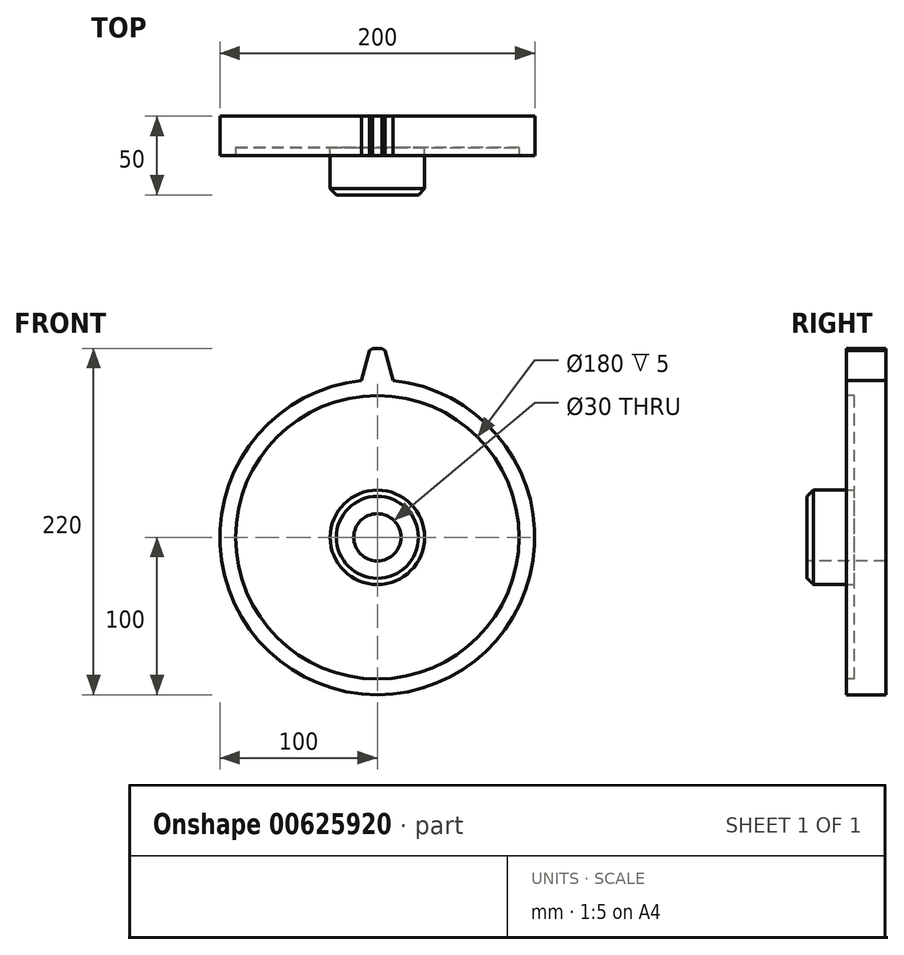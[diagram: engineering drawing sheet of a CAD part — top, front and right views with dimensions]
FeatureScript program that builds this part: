
annotation { "Feature Type Name" : "Feature", "Feature Type Description" : "" }
export const myFeature = defineFeature(function(context is Context, id is Id, definition is map)
    precondition{}
    {
        {
            var Q0;
            Q0=qCreatedBy(makeId("Front.planeOp"),FACE);
            var sketch = newSketch(context, id + "F0", { "sketchPlane" : qUnion([Q0])});
            skCircle(sketch, "E0", {"center": v(0, 0) * mm, "radius": 100 * mm});
            skSolve(sketch);
        }
        {
            var Q0;
            Q0 = qSketchRegion(id + "F0", true);
            extrude(context, id + "F1", {"entities" : qUnion([Q0]), "depth" : 25 * mm, "offsetDistance" : 25 * mm});
        }
        {
            var Q0;
            Q0=makeQuery(id+"F1.opExtrude","CAP_FACE",FACE,{"disambiguationData":[OSD([sQuery(id+"F0.wireOp",EDGE,"E0")])],"isStart":false});
            var sketch = newSketch(context, id + "F2", { "sketchPlane" : qUnion([Q0])});
            skCircle(sketch, "E1", {"center": v(0, 0) * mm, "radius": 120 * mm, "construction": true});
            skLineSegment(sketch, "E2", {"start": v(4.5, 120) * mm, "end": v(-4.5, 120) * mm});
            skPoint(sketch, "E3", {"position": v(0, 120) * mm});
            skLineSegment(sketch, "E4", {"start": v(-4.5, 120) * mm, "end": v(-10, 99.5) * mm});
            skLineSegment(sketch, "E5", {"start": v(4.5, 120) * mm, "end": v(10, 99.5) * mm});
            skLineSegment(sketch, "E6", {"start": v(-10, 99.5) * mm, "end": v(10, 99.5) * mm});
            skSolve(sketch);
        }
        {
            var Q0;
            Q0=makeQuery(id+"F2.imprint","IMPRINT",FACE,{"disambiguationData":[TD([[makeQuery(id+"F2.imprint","IMPRINT",EDGE,{"derivedFrom":sQuery(id+"F2.wireOp",EDGE,"E2")}),1.0]])]});
            extrude(context, id + "F3", {"entities" : qUnion([Q0]), "operationType" : NewBodyOperationType.ADD, "oppositeDirection" : true, "depth" : 25 * mm, "offsetDistance" : 25 * mm});
        }
        {
            var Q0;
            Q0=makeQuery(id+"F3.opExtrude","SWEPT_EDGE",EDGE,{"disambiguationData":[OSD([sQuery(id+"F2.wireOp",EDGE,"E2"),sQuery(id+"F2.wireOp",EDGE,"E5")])]});
            var Q1;
            Q1=makeQuery(id+"F3.opExtrude","SWEPT_EDGE",EDGE,{"disambiguationData":[OSD([sQuery(id+"F2.wireOp",EDGE,"E2"),sQuery(id+"F2.wireOp",EDGE,"E4")])]});
            chamfer(context, id + "F4", {"entities" : qUnion([Q0, Q1]), "width" : 2 * mm, "tangentPropagation" : true});
        }
        {
            var Q0;
            Q0=makeQuery(id+"F3.opExtrude","SWEPT_EDGE",EDGE,{"disambiguationData":[OSD([sQuery(id+"F0.wireOp",EDGE,"E0"),sQuery(id+"F2.wireOp",EDGE,"E4"),sQuery(id+"F2.wireOp",EDGE,"E6")])]});
            var Q1;
            Q1=makeQuery(id+"F3.opExtrude","SWEPT_EDGE",EDGE,{"disambiguationData":[OSD([sQuery(id+"F0.wireOp",EDGE,"E0"),sQuery(id+"F2.wireOp",EDGE,"E5"),sQuery(id+"F2.wireOp",EDGE,"E6")])]});
            fillet(context, id + "F5", {"entities" : qUnion([Q0, Q1]), "radius" : 5 * mm, "tangentPropagation" : true, "allowEdgeOverflow" : false});
        }
        {
            var Q0;
            {var subQ0=sQuery(id+"F2.wireOp",EDGE,"E5");var subQ1=sQuery(id+"F2.wireOp",EDGE,"E4");var subQ2=sQuery(id+"F2.wireOp",EDGE,"E2");var subQ3=sQuery(id+"F0.wireOp",EDGE,"E0");Q0=makeQuery(id+"F1aVIN3etHBw0Ek_1.19.F3.boolean.opBoolean","MERGE",FACE,{"derivedFrom":[makeQuery(id+"F1aVIN3etHBw0Ek_1.18.F3.boolean.opBoolean","MERGE",FACE,{"derivedFrom":[makeQuery(id+"F1aVIN3etHBw0Ek_1.17.F3.boolean.opBoolean","MERGE",FACE,{"derivedFrom":[makeQuery(id+"F1aVIN3etHBw0Ek_1.16.F3.boolean.opBoolean","MERGE",FACE,{"derivedFrom":[makeQuery(id+"F1aVIN3etHBw0Ek_1.15.F3.boolean.opBoolean","MERGE",FACE,{"derivedFrom":[makeQuery(id+"F1aVIN3etHBw0Ek_1.14.F3.boolean.opBoolean","MERGE",FACE,{"derivedFrom":[makeQuery(id+"F1aVIN3etHBw0Ek_1.13.F3.boolean.opBoolean","MERGE",FACE,{"derivedFrom":[makeQuery(id+"F1aVIN3etHBw0Ek_1.12.F3.boolean.opBoolean","MERGE",FACE,{"derivedFrom":[makeQuery(id+"F1aVIN3etHBw0Ek_1.11.F3.boolean.opBoolean","MERGE",FACE,{"derivedFrom":[makeQuery(id+"F1aVIN3etHBw0Ek_1.10.F3.boolean.opBoolean","MERGE",FACE,{"derivedFrom":[makeQuery(id+"F1aVIN3etHBw0Ek_1.9.F3.boolean.opBoolean","MERGE",FACE,{"derivedFrom":[makeQuery(id+"F1aVIN3etHBw0Ek_1.8.F3.boolean.opBoolean","MERGE",FACE,{"derivedFrom":[makeQuery(id+"F1aVIN3etHBw0Ek_1.7.F3.boolean.opBoolean","MERGE",FACE,{"derivedFrom":[makeQuery(id+"F1aVIN3etHBw0Ek_1.6.F3.boolean.opBoolean","MERGE",FACE,{"derivedFrom":[makeQuery(id+"F1aVIN3etHBw0Ek_1.5.F3.boolean.opBoolean","MERGE",FACE,{"derivedFrom":[makeQuery(id+"F1aVIN3etHBw0Ek_1.4.F3.boolean.opBoolean","MERGE",FACE,{"derivedFrom":[makeQuery(id+"F1aVIN3etHBw0Ek_1.3.F3.boolean.opBoolean","MERGE",FACE,{"derivedFrom":[makeQuery(id+"F1aVIN3etHBw0Ek_1.2.F3.boolean.opBoolean","MERGE",FACE,{"derivedFrom":[makeQuery(id+"F1aVIN3etHBw0Ek_1.1.F3.boolean.opBoolean","MERGE",FACE,{"derivedFrom":[makeQuery(id+"F3.boolean.opBoolean","MERGE",FACE,{"derivedFrom":[makeQuery(id+"F1.opExtrude","CAP_FACE",FACE,{"disambiguationData":[OSD([subQ3])],"isStart":false}),makeQuery(id+"F3.opExtrude","CAP_FACE",FACE,{"disambiguationData":[OSD([subQ3,subQ2,subQ1,subQ0])],"isStart":true})]}),makeQuery(id+"F1aVIN3etHBw0Ek_1.1.F3.opExtrude","CAP_FACE",FACE,{"disambiguationData":[OSD([subQ3,subQ2,subQ1,subQ0])],"isStart":true})]}),makeQuery(id+"F1aVIN3etHBw0Ek_1.2.F3.opExtrude","CAP_FACE",FACE,{"disambiguationData":[OSD([subQ3,subQ2,subQ1,subQ0])],"isStart":true})]}),makeQuery(id+"F1aVIN3etHBw0Ek_1.3.F3.opExtrude","CAP_FACE",FACE,{"disambiguationData":[OSD([subQ3,subQ2,subQ1,subQ0])],"isStart":true})]}),makeQuery(id+"F1aVIN3etHBw0Ek_1.4.F3.opExtrude","CAP_FACE",FACE,{"disambiguationData":[OSD([subQ3,subQ2,subQ1,subQ0])],"isStart":true})]}),makeQuery(id+"F1aVIN3etHBw0Ek_1.5.F3.opExtrude","CAP_FACE",FACE,{"disambiguationData":[OSD([subQ3,subQ2,subQ1,subQ0])],"isStart":true})]}),makeQuery(id+"F1aVIN3etHBw0Ek_1.6.F3.opExtrude","CAP_FACE",FACE,{"disambiguationData":[OSD([subQ3,subQ2,subQ1,subQ0])],"isStart":true})]}),makeQuery(id+"F1aVIN3etHBw0Ek_1.7.F3.opExtrude","CAP_FACE",FACE,{"disambiguationData":[OSD([subQ3,subQ2,subQ1,subQ0])],"isStart":true})]}),makeQuery(id+"F1aVIN3etHBw0Ek_1.8.F3.opExtrude","CAP_FACE",FACE,{"disambiguationData":[OSD([subQ3,subQ2,subQ1,subQ0])],"isStart":true})]}),makeQuery(id+"F1aVIN3etHBw0Ek_1.9.F3.opExtrude","CAP_FACE",FACE,{"disambiguationData":[OSD([subQ3,subQ2,subQ1,subQ0])],"isStart":true})]}),makeQuery(id+"F1aVIN3etHBw0Ek_1.10.F3.opExtrude","CAP_FACE",FACE,{"disambiguationData":[OSD([subQ3,subQ2,subQ1,subQ0])],"isStart":true})]}),makeQuery(id+"F1aVIN3etHBw0Ek_1.11.F3.opExtrude","CAP_FACE",FACE,{"disambiguationData":[OSD([subQ3,subQ2,subQ1,subQ0])],"isStart":true})]}),makeQuery(id+"F1aVIN3etHBw0Ek_1.12.F3.opExtrude","CAP_FACE",FACE,{"disambiguationData":[OSD([subQ3,subQ2,subQ1,subQ0])],"isStart":true})]}),makeQuery(id+"F1aVIN3etHBw0Ek_1.13.F3.opExtrude","CAP_FACE",FACE,{"disambiguationData":[OSD([subQ3,subQ2,subQ1,subQ0])],"isStart":true})]}),makeQuery(id+"F1aVIN3etHBw0Ek_1.14.F3.opExtrude","CAP_FACE",FACE,{"disambiguationData":[OSD([subQ3,subQ2,subQ1,subQ0])],"isStart":true})]}),makeQuery(id+"F1aVIN3etHBw0Ek_1.15.F3.opExtrude","CAP_FACE",FACE,{"disambiguationData":[OSD([subQ3,subQ2,subQ1,subQ0])],"isStart":true})]}),makeQuery(id+"F1aVIN3etHBw0Ek_1.16.F3.opExtrude","CAP_FACE",FACE,{"disambiguationData":[OSD([subQ3,subQ2,subQ1,subQ0])],"isStart":true})]}),makeQuery(id+"F1aVIN3etHBw0Ek_1.17.F3.opExtrude","CAP_FACE",FACE,{"disambiguationData":[OSD([subQ3,subQ2,subQ1,subQ0])],"isStart":true})]}),makeQuery(id+"F1aVIN3etHBw0Ek_1.18.F3.opExtrude","CAP_FACE",FACE,{"disambiguationData":[OSD([subQ3,subQ2,subQ1,subQ0])],"isStart":true})]}),makeQuery(id+"F1aVIN3etHBw0Ek_1.19.F3.opExtrude","CAP_FACE",FACE,{"disambiguationData":[OSD([subQ3,subQ2,subQ1,subQ0])],"isStart":true})]});}
            var sketch = newSketch(context, id + "F6", { "sketchPlane" : qUnion([Q0])});
            skCircle(sketch, "E7", {"center": v(0, 0) * mm, "radius": 90 * mm});
            skSolve(sketch);
        }
        {
            var Q0;
            Q0 = qSketchRegion(id + "F6", true);
            extrude(context, id + "F7", {"entities" : qUnion([Q0]), "operationType" : NewBodyOperationType.REMOVE, "oppositeDirection" : true, "depth" : 5 * mm, "offsetDistance" : 25 * mm});
        }
        {
            var Q0;
            Q0=makeQuery(id+"F7.boolean.opBoolean","COPY",FACE,{"derivedFrom":makeQuery(id+"F7.opExtrude","CAP_FACE",FACE,{"disambiguationData":[OSD([sQuery(id+"F6.wireOp",EDGE,"E7")])],"isStart":false})});
            var sketch = newSketch(context, id + "F8", { "sketchPlane" : qUnion([Q0])});
            skCircle(sketch, "E8", {"center": v(0, 0) * mm, "radius": 30 * mm});
            skSolve(sketch);
        }
        {
            var Q0;
            Q0 = qSketchRegion(id + "F8", true);
            extrude(context, id + "F9", {"entities" : qUnion([Q0]), "operationType" : NewBodyOperationType.ADD, "depth" : 30 * mm, "offsetDistance" : 25 * mm});
        }
        {
            var Q0;
            Q0=makeQuery(id+"F9.opExtrude","CAP_FACE",FACE,{"disambiguationData":[OSD([sQuery(id+"F8.wireOp",EDGE,"E8")])],"isStart":false});
            var sketch = newSketch(context, id + "F10", { "sketchPlane" : qUnion([Q0])});
            skCircle(sketch, "E9", {"center": v(0, 0) * mm, "radius": 15 * mm});
            skSolve(sketch);
        }
        {
            var Q0;
            Q0 = qSketchRegion(id + "F10", true);
            extrude(context, id + "F11", {"entities" : qUnion([Q0]), "operationType" : NewBodyOperationType.REMOVE, "endBound" : BoundingType.THROUGH_ALL, "oppositeDirection" : true, "depth" : 25 * mm, "offsetDistance" : 25 * mm});
        }
        {
            var Q0;
            Q0=makeQuery(id+"F9.opExtrude","CAP_EDGE",EDGE,{"disambiguationData":[OSD([sQuery(id+"F8.wireOp",EDGE,"E8")])],"isStart":false});
            var Q1;
            Q1=makeQuery(id+"F11.boolean.opBoolean","COPY",EDGE,{"derivedFrom":makeQuery(id+"F11.opExtrude","CAP_EDGE",EDGE,{"disambiguationData":[OSD([sQuery(id+"F10.wireOp",EDGE,"E9")])],"isStart":true})});
            chamfer(context, id + "F12", {"entities" : qUnion([Q0, Q1]), "width" : 4 * mm, "tangentPropagation" : true});
        }
    });
